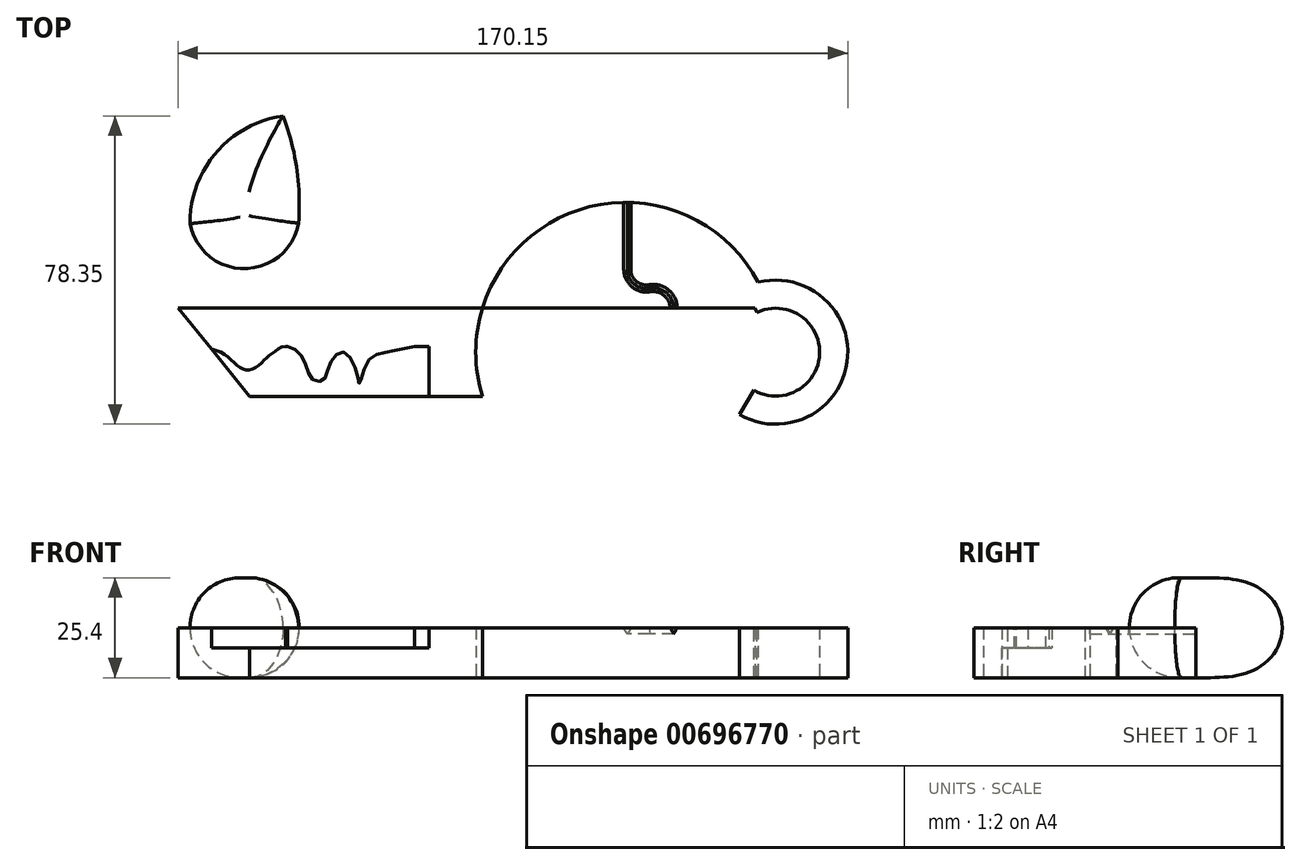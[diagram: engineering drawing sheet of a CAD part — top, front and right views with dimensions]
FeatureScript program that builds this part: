
annotation { "Feature Type Name" : "Feature", "Feature Type Description" : "" }
export const myFeature = defineFeature(function(context is Context, id is Id, definition is map)
    precondition{}
    {
        {
            var Q0;
            Q0=qCreatedBy(makeId("Top.planeOp"),FACE);
            var sketch = newSketch(context, id + "F0", { "sketchPlane" : qUnion([Q0])});
            skLineSegment(sketch, "E0", {"start": v(-76.55, 0) * mm, "end": v(76.12, 0) * mm});
            skLineSegment(sketch, "E1", {"start": v(0, 77.38) * mm, "end": v(0, -75.9) * mm});
            skLineSegment(sketch, "E2", {"start": v(0, 0) * mm, "end": v(76.12, 0) * mm});
            skLineSegment(sketch, "E3", {"start": v(38.06, 0) * mm, "end": v(38.06, 75.69) * mm});
            skCircle(sketch, "E4", {"center": v(38.06, 0) * mm, "radius": 38.06 * mm});
            skLineSegment(sketch, "E5.bottom", {"start": v(-75.64, 11.2) * mm, "end": v(74.43, 11.2) * mm});
            skLineSegment(sketch, "E5.top", {"start": v(-75.64, -11.2) * mm, "end": v(1.69, -11.2) * mm});
            skLineSegment(sketch, "E5.left", {"start": v(-75.64, 11.2) * mm, "end": v(-75.64, -11.2) * mm});
            skPoint(sketch, "E5.middle", {"position": v(0, 0) * mm});
            skCircle(sketch, "E6", {"center": v(48.41, -22.16) * mm, "radius": 17.71 * mm});
            skCircle(sketch, "E7.cCircle", {"center": v(15.13, -16.3) * mm, "radius": 9.61 * mm, "construction": true});
            skLineSegment(sketch, "E7.0", {"start": v(20.42, -7.35) * mm, "end": v(25.2, -13.71) * mm});
            skLineSegment(sketch, "E7.1", {"start": v(25.2, -13.71) * mm, "end": v(24.09, -21.6) * mm});
            skLineSegment(sketch, "E7.2", {"start": v(24.09, -21.6) * mm, "end": v(17.72, -26.38) * mm});
            skLineSegment(sketch, "E7.3", {"start": v(17.72, -26.38) * mm, "end": v(9.84, -25.26) * mm});
            skLineSegment(sketch, "E7.4", {"start": v(9.84, -25.26) * mm, "end": v(5.05, -18.9) * mm});
            skLineSegment(sketch, "E7.5", {"start": v(5.05, -18.9) * mm, "end": v(6.17, -11.01) * mm});
            skLineSegment(sketch, "E7.6", {"start": v(6.17, -11.01) * mm, "end": v(12.54, -6.23) * mm});
            skLineSegment(sketch, "E7.7", {"start": v(12.54, -6.23) * mm, "end": v(20.42, -7.35) * mm});
            skPoint(sketch, "E7.0.midPoint", {"position": v(22.81, -10.53) * mm});
            skArc(sketch, "E8", {"start": v(-48.97, 60.04) * mm, "mid": v(-65.9, 50.77) * mm, "end": v(-72.61, 32.66) * mm});
            skArc(sketch, "E9", {"start": v(-45.03, 32.74) * mm, "mid": v(-45.48, 46.61) * mm, "end": v(-48.97, 60.04) * mm});
            skArc(sketch, "E10", {"start": v(-72.61, 32.66) * mm, "mid": v(-58.79, 21.21) * mm, "end": v(-45.03, 32.74) * mm});
            skSolve(sketch);
        }
        {
            var Q0;
            {var subQ0=sQuery(id+"F0.wireOp",EDGE,"E4");var subQ1=sQuery(id+"F0.wireOp",EDGE,"E3");var subQ2=makeQuery(id+"F0.imprint","INTERSECT",VERTEX,{"derivedFrom":[subQ1,subQ0]});Q0=makeQuery(id+"F0.imprint","IMPRINT",FACE,{"disambiguationData":[TD([[makeQuery(id+"F0.imprint","IMPRINT",EDGE,{"disambiguationData":[TD([[subQ2,1.0]])],"derivedFrom":subQ1}),1.0]])]});}
            var Q1;
            {var subQ0=sQuery(id+"F0.wireOp",EDGE,"E4");var subQ1=sQuery(id+"F0.wireOp",EDGE,"E3");var subQ2=makeQuery(id+"F0.imprint","INTERSECT",VERTEX,{"derivedFrom":[subQ1,subQ0]});Q1=makeQuery(id+"F0.imprint","IMPRINT",FACE,{"disambiguationData":[TD([[makeQuery(id+"F0.imprint","IMPRINT",EDGE,{"disambiguationData":[TD([[subQ2,1.0]])],"derivedFrom":subQ1}),-1.0]])]});}
            var Q2;
            {var subQ0=sQuery(id+"F0.wireOp",EDGE,"E4");var subQ1=sQuery(id+"F0.wireOp",EDGE,"E2");var subQ2=makeQuery(id+"F0.imprint","INTERSECT",VERTEX,{"derivedFrom":[subQ1,subQ0]});Q2=makeQuery(id+"F0.imprint","IMPRINT",FACE,{"disambiguationData":[TD([[makeQuery(id+"F0.imprint","IMPRINT",EDGE,{"disambiguationData":[TD([[subQ2,1.0]])],"derivedFrom":subQ1}),1.0]])]});}
            var Q3;
            {var subQ1=sQuery(id+"F0.wireOp",EDGE,"E2");var subQ3=sQuery(id+"F0.wireOp",EDGE,"E3");var subQ4=makeQuery(id+"F0.imprint","INTERSECT",VERTEX,{"derivedFrom":[subQ1,subQ3]});Q3=makeQuery(id+"F0.imprint","IMPRINT",FACE,{"disambiguationData":[TD([[makeQuery(id+"F0.imprint","IMPRINT",EDGE,{"disambiguationData":[TD([[subQ4,-1.0]])],"derivedFrom":subQ3}),1.0]])]});}
            var Q4;
            {var subQ0=sQuery(id+"F0.wireOp",EDGE,"E4");var subQ1=sQuery(id+"F0.wireOp",EDGE,"E2");var subQ4=makeQuery(id+"F0.imprint","INTERSECT",VERTEX,{"derivedFrom":[subQ1,subQ0]});Q4=makeQuery(id+"F0.imprint","IMPRINT",FACE,{"disambiguationData":[TD([[makeQuery(id+"F0.imprint","IMPRINT",EDGE,{"disambiguationData":[TD([[subQ4,1.0]])],"derivedFrom":subQ1}),-1.0]])]});}
            var Q5;
            {var subQ3=sQuery(id+"F0.wireOp",EDGE,"E5.left");var subQ5=sQuery(id+"F0.wireOp",EDGE,"E5.top");var subQ6=makeQuery(id+"F0.imprint","INTERSECT",VERTEX,{"derivedFrom":[subQ5,subQ3]});Q5=makeQuery(id+"F0.imprint","IMPRINT",FACE,{"disambiguationData":[TD([[makeQuery(id+"F0.imprint","IMPRINT",EDGE,{"disambiguationData":[TD([[subQ6,-1.0]])],"derivedFrom":subQ5}),1.0]])]});}
            var Q6;
            {var subQ3=sQuery(id+"F0.wireOp",EDGE,"E5.left");var subQ5=sQuery(id+"F0.wireOp",EDGE,"E5.bottom");var subQ7=makeQuery(id+"F0.imprint","INTERSECT",VERTEX,{"derivedFrom":[subQ5,subQ3]});Q6=makeQuery(id+"F0.imprint","IMPRINT",FACE,{"disambiguationData":[TD([[makeQuery(id+"F0.imprint","IMPRINT",EDGE,{"disambiguationData":[TD([[subQ7,-1.0]])],"derivedFrom":subQ5}),-1.0]])]});}
            var Q7;
            {var subQ1=sQuery(id+"F0.wireOp",EDGE,"E1");var subQ3=sQuery(id+"F0.wireOp",EDGE,"E5.bottom");var subQ4=makeQuery(id+"F0.imprint","INTERSECT",VERTEX,{"derivedFrom":[subQ1,subQ3]});Q7=makeQuery(id+"F0.imprint","IMPRINT",FACE,{"disambiguationData":[TD([[makeQuery(id+"F0.imprint","IMPRINT",EDGE,{"disambiguationData":[TD([[subQ4,-1.0]])],"derivedFrom":subQ3}),-1.0]])]});}
            var Q8;
            {var subQ0=sQuery(id+"F0.wireOp",EDGE,"E4");var subQ3=sQuery(id+"F0.wireOp",EDGE,"E5.top");var subQ5=makeQuery(id+"F0.imprint","INTERSECT",VERTEX,{"derivedFrom":[subQ0,subQ3]});Q8=makeQuery(id+"F0.imprint","IMPRINT",FACE,{"disambiguationData":[TD([[makeQuery(id+"F0.imprint","IMPRINT",EDGE,{"disambiguationData":[TD([[subQ5,1.0]])],"derivedFrom":subQ3}),1.0]])]});}
            extrude(context, id + "F1", {"entities" : qUnion([Q0, Q1, Q2, Q3, Q4, Q5, Q6, Q7, Q8]), "depth" : 12.7 * mm, "offsetDistance" : 25.4 * mm});
        }
        {
            var Q0;
            Q0=makeQuery(id+"F1.opExtrude","SWEPT_FACE",FACE,{"disambiguationData":[OSD([sQuery(id+"F0.wireOp",EDGE,"E5.top")])]});
            var sketch = newSketch(context, id + "F2", { "sketchPlane" : qUnion([Q0])});
            skPoint(sketch, "E11.oppositeSnap0", {"position": v(1.69, 6.35) * mm});
            skLineSegment(sketch, "E12.bottom", {"start": v(-75.64, 12.7) * mm, "end": v(-11.84, 12.7) * mm});
            skLineSegment(sketch, "E12.top", {"start": v(-75.64, 7.53) * mm, "end": v(-11.84, 7.53) * mm});
            skLineSegment(sketch, "E12.left", {"start": v(-75.64, 12.7) * mm, "end": v(-75.64, 7.53) * mm});
            skLineSegment(sketch, "E12.right", {"start": v(-11.84, 12.7) * mm, "end": v(-11.84, 7.53) * mm});
            skSolve(sketch);
        }
        {
            var Q0;
            Q0=qSketchRegion(id+"F2",true);
            extrude(context, id + "F3", {"entities" : qUnion([Q0]), "operationType" : NewBodyOperationType.REMOVE, "oppositeDirection" : true, "depth" : 12.7 * mm, "offsetDistance" : 25.4 * mm});
        }
        {
            var Q0;
            Q0=makeQuery(id+"F3.boolean.opBoolean","COPY",FACE,{"derivedFrom":makeQuery(id+"F3.opExtrude","SWEPT_FACE",FACE,{"disambiguationData":[OSD([sQuery(id+"F2.wireOp",EDGE,"E12.top")])]})});
            var sketch = newSketch(context, id + "F4", { "sketchPlane" : qUnion([Q0])});
            skPoint(sketch, "E13.8.internal.snap0", {"position": v(-43.74, 1.5) * mm});
            skFitSpline(sketch, "E13", {"points": [v(-71.4, 1.5) * mm, v(-64.86, 0) * mm, v(-61.37, -2.73) * mm, v(-58.75, -4.47) * mm, v(-56.14, -4.03) * mm, v(-53.52, -1.85) * mm, v(-51.34, 0) * mm, v(-47.85, 1.5) * mm, v(-43.74, -1.85) * mm, v(-41.75, -6.65) * mm, v(-38.7, -7.09) * mm, v(-36.95, -2.73) * mm, v(-33.46, 0) * mm, v(-29.98, -6.21) * mm, v(-29.54, -7.96) * mm, v(-27.36, -2.29) * mm, v(-22.56, 0) * mm, v(-15.59, 1.5) * mm], "startDerivative": vector(98.42, -12.85) * mm, "endDerivative": vector(95.91, 21.9) * mm});
            skLineSegment(sketch, "E14", {"start": v(-71.4, 1.5) * mm, "end": v(-15.59, 1.5) * mm});
            skSolve(sketch);
        }
        {
            var Q0;
            {var subQ0=sQuery(id+"F4.wireOp",EDGE,"E14");var subQ1=sQuery(id+"F4.wireOp",EDGE,"E13");var subQ3=makeQuery(id+"F4.imprint","INTERSECT",VERTEX,{"disambiguationData":[OD(0.0)],"derivedFrom":[subQ1,subQ0]});Q0=makeQuery(id+"F4.imprint","IMPRINT",FACE,{"disambiguationData":[TD([[makeQuery(id+"F4.imprint","IMPRINT",EDGE,{"disambiguationData":[TD([[subQ3,1.0]])],"derivedFrom":subQ1}),1.0]])]});}
            var Q1;
            {var subQ0=sQuery(id+"F4.wireOp",EDGE,"E14");var subQ1=sQuery(id+"F4.wireOp",EDGE,"E13");var subQ3=makeQuery(id+"F4.imprint","INTERSECT",VERTEX,{"disambiguationData":[OD(1.0)],"derivedFrom":[subQ1,subQ0]});Q1=makeQuery(id+"F4.imprint","IMPRINT",FACE,{"disambiguationData":[TD([[makeQuery(id+"F4.imprint","IMPRINT",EDGE,{"disambiguationData":[TD([[subQ3,-1.0]])],"derivedFrom":subQ1}),1.0]])]});}
            var Q2;
            Q2=makeQuery(id+"F1.opExtrude","CAP_FACE",FACE,{"disambiguationData":[OSD([sQuery(id+"F0.wireOp",EDGE,"E4"),sQuery(id+"F0.wireOp",EDGE,"E5.bottom"),sQuery(id+"F0.wireOp",EDGE,"E5.top"),sQuery(id+"F0.wireOp",EDGE,"E5.left")])],"isStart":false});
            extrude(context, id + "F5", {"entities" : qUnion([Q0, Q1]), "operationType" : NewBodyOperationType.ADD, "endBound" : BoundingType.UP_TO_SURFACE, "depth" : 25.4 * mm, "endBoundEntityFace" : qUnion([Q2]), "offsetDistance" : 25.4 * mm});
        }
        {
            var Q0;
            {var subQ0=sQuery(id+"F0.wireOp",EDGE,"E5.left");var subQ1=sQuery(id+"F0.wireOp",EDGE,"E5.top");var subQ2=sQuery(id+"F0.wireOp",EDGE,"E5.bottom");var subQ3=sQuery(id+"F0.wireOp",EDGE,"E4");Q0=makeQuery(id+"F5.boolean.opBoolean","MERGE",FACE,{"derivedFrom":[makeQuery(id+"F1.opExtrude","CAP_FACE",FACE,{"disambiguationData":[OSD([subQ3,subQ2,subQ1,subQ0])],"isStart":false}),makeQuery(id+"F5.opExtrude","CAP_FACE",FACE,{"disambiguationData":[OSD([subQ3,subQ2,subQ1,subQ0]),OD(0.0)],"isStart":false}),makeQuery(id+"F5.opExtrude","CAP_FACE",FACE,{"disambiguationData":[OSD([subQ3,subQ2,subQ1,subQ0]),OD(1.0)],"isStart":false})]});}
            var sketch = newSketch(context, id + "F6", { "sketchPlane" : qUnion([Q0])});
            skLineSegment(sketch, "E15", {"start": v(-54.4, -14.93) * mm, "end": v(-80.56, -12.75) * mm});
            skLineSegment(sketch, "E16", {"start": v(-80.56, -12.75) * mm, "end": v(-75.64, 11.2) * mm});
            skLineSegment(sketch, "E17", {"start": v(-75.64, 11.2) * mm, "end": v(-54.4, -14.93) * mm});
            skSolve(sketch);
        }
        {
            var Q0;
            Q0=qSketchRegion(id+"F6",true);
            extrude(context, id + "F7", {"entities" : qUnion([Q0]), "operationType" : NewBodyOperationType.REMOVE, "endBound" : BoundingType.THROUGH_ALL, "oppositeDirection" : true, "depth" : 25.4 * mm, "offsetDistance" : 25.4 * mm});
        }
        {
            var Q0;
            Q0=qCreatedBy(makeId("Right.planeOp"),FACE);
            cPlane(context, id + "F8", {"entities" : qUnion([Q0]), "cplaneType" : CPlaneType.OFFSET, "offset" : 76.2 * mm, "width" : 152.4 * mm, "height" : 152.4 * mm});
        }
        {
            var Q0;
            Q0=qCreatedBy(id+"F8.planeOp",FACE);
            var sketch = newSketch(context, id + "F9", { "sketchPlane" : qUnion([Q0])});
            skLineSegment(sketch, "E18", {"start": v(0, -5.67) * mm, "end": v(0, 19.48) * mm});
            skLineSegment(sketch, "E19.top", {"start": v(11.16, 0) * mm, "end": v(18.3, 0) * mm});
            skLineSegment(sketch, "E20", {"start": v(11.16, 0) * mm, "end": v(11.16, 12.7) * mm});
            skLineSegment(sketch, "E21", {"start": v(11.16, 12.7) * mm, "end": v(18.3, 12.7) * mm});
            skLineSegment(sketch, "E22", {"start": v(18.3, 12.7) * mm, "end": v(18.3, 0) * mm});
            skSolve(sketch);
        }
        {
            var Q0;
            Q0=makeQuery(id+"F9.imprint","IMPRINT",FACE,{"disambiguationData":[TD([[makeQuery(id+"F9.imprint","IMPRINT",EDGE,{"derivedFrom":sQuery(id+"F9.wireOp",EDGE,"E19.top")}),1.0]])]});
            var Q1;
            Q1=sQuery(id+"F9.wireOp",EDGE,"E18");
            revolve(context, id + "F10", {"operationType" : NewBodyOperationType.ADD, "entities" : qUnion([Q0]), "axis" : qUnion([Q1]), "revolveType" : RevolveType.TWO_DIRECTIONS, "angle" : 25 * degree, "angleBack" : 150 * degree});
        }
        {
            var Q0;
            Q0=qCreatedBy(makeId("Front.planeOp"),FACE);
            cPlane(context, id + "F11", {"entities" : qUnion([Q0]), "cplaneType" : CPlaneType.OFFSET, "offset" : 38.1 * mm, "width" : 152.4 * mm, "height" : 152.4 * mm});
        }
        {
            var Q0;
            {var subQ0=sQuery(id+"F0.wireOp",EDGE,"E5.left");var subQ1=sQuery(id+"F0.wireOp",EDGE,"E5.top");var subQ2=sQuery(id+"F0.wireOp",EDGE,"E5.bottom");var subQ3=sQuery(id+"F0.wireOp",EDGE,"E4");Q0=makeQuery(id+"F5.boolean.opBoolean","MERGE",FACE,{"derivedFrom":[makeQuery(id+"F1.opExtrude","CAP_FACE",FACE,{"disambiguationData":[OSD([subQ3,subQ2,subQ1,subQ0])],"isStart":false}),makeQuery(id+"F5.opExtrude","CAP_FACE",FACE,{"disambiguationData":[OSD([subQ3,subQ2,subQ1,subQ0]),OD(0.0)],"isStart":false}),makeQuery(id+"F5.opExtrude","CAP_FACE",FACE,{"disambiguationData":[OSD([subQ3,subQ2,subQ1,subQ0]),OD(1.0)],"isStart":false})]});}
            var sketch = newSketch(context, id + "F12", { "sketchPlane" : qUnion([Q0])});
            skLineSegment(sketch, "E23", {"start": v(38.5, -38.06) * mm, "end": v(38.5, -21.04) * mm});
            skArc(sketch, "E24", {"start": v(38.5, -21.04) * mm, "mid": v(40.22, -17.32) * mm, "end": v(44.17, -16.24) * mm});
            skArc(sketch, "E25", {"start": v(44.17, -16.24) * mm, "mid": v(48.62, -14.91) * mm, "end": v(50.28, -10.57) * mm});
            skLineSegment(sketch, "E26", {"start": v(50.28, -10.57) * mm, "end": v(50.28, 0) * mm});
            skLineSegment(sketch, "E27", {"start": v(0, 0) * mm, "end": v(43.3, 0) * mm});
            skLineSegment(sketch, "E28.MirrorCS", {"start": v(50.28, 10.57) * mm, "end": v(50.28, 0) * mm});
            skArc(sketch, "E29.MirrorCS", {"start": v(44.17, 16.24) * mm, "mid": v(48.62, 14.91) * mm, "end": v(50.28, 10.57) * mm});
            skArc(sketch, "E30.MirrorCS", {"start": v(38.5, 21.04) * mm, "mid": v(40.22, 17.32) * mm, "end": v(44.17, 16.24) * mm});
            skLineSegment(sketch, "E31.MirrorCS", {"start": v(38.5, 38.06) * mm, "end": v(38.5, 21.04) * mm});
            skSolve(sketch);
        }
        {
            var Q0;
            Q0=qCreatedBy(id+"F11.planeOp",FACE);
            var sketch = newSketch(context, id + "F13", { "sketchPlane" : qUnion([Q0])});
            skCircle(sketch, "E32.cCircle", {"center": v(38.5, 12.73) * mm, "radius": 1.6 * mm, "construction": true});
            skLineSegment(sketch, "E32.0", {"start": v(38.5, 11.14) * mm, "end": v(37.1, 13.53) * mm});
            skLineSegment(sketch, "E32.1", {"start": v(37.1, 13.53) * mm, "end": v(39.87, 13.53) * mm});
            skLineSegment(sketch, "E32.2", {"start": v(39.87, 13.53) * mm, "end": v(38.5, 11.14) * mm});
            skSolve(sketch);
        }
        {
            var Q0;
            Q0=makeQuery(id+"F13.imprint","IMPRINT",FACE,{"disambiguationData":[TD([[makeQuery(id+"F13.imprint","IMPRINT",EDGE,{"derivedFrom":sQuery(id+"F13.wireOp",EDGE,"E32.0")}),-1.0]])]});
            var Q1;
            Q1=sQuery(id+"F12.wireOp",EDGE,"E23");
            var Q2;
            Q2=sQuery(id+"F12.wireOp",EDGE,"E24");
            var Q3;
            Q3=sQuery(id+"F12.wireOp",EDGE,"E25");
            var Q4;
            Q4=sQuery(id+"F12.wireOp",EDGE,"E26");
            var Q5;
            Q5=sQuery(id+"F12.wireOp",EDGE,"E28.MirrorCS");
            var Q6;
            Q6=sQuery(id+"F12.wireOp",EDGE,"E29.MirrorCS");
            var Q7;
            Q7=sQuery(id+"F12.wireOp",EDGE,"E30.MirrorCS");
            var Q8;
            Q8=sQuery(id+"F12.wireOp",EDGE,"E31.MirrorCS");
            sweep(context, id + "F14", {"operationType" : NewBodyOperationType.REMOVE, "profiles" : qUnion([Q0]), "path" : qUnion([Q1, Q2, Q3, Q4, Q5, Q6, Q7, Q8])});
        }
        {
            var Q0;
            Q0=makeQuery(id+"F0.imprint","IMPRINT",FACE,{"disambiguationData":[TD([[makeQuery(id+"F0.imprint","IMPRINT",EDGE,{"derivedFrom":sQuery(id+"F0.wireOp",EDGE,"E8")}),1.0]])]});
            extrude(context, id + "F15", {"entities" : qUnion([Q0]), "depth" : 25.4 * mm, "offsetDistance" : 25.4 * mm});
        }
        {
            var Q0;
            Q0=makeQuery(id+"F15.opExtrude","CAP_FACE",FACE,{"disambiguationData":[OSD([sQuery(id+"F0.wireOp",EDGE,"E8"),sQuery(id+"F0.wireOp",EDGE,"E9"),sQuery(id+"F0.wireOp",EDGE,"E10")])],"isStart":false});
            var Q1;
            Q1=makeQuery(id+"F15.opExtrude","CAP_FACE",FACE,{"disambiguationData":[OSD([sQuery(id+"F0.wireOp",EDGE,"E8"),sQuery(id+"F0.wireOp",EDGE,"E9"),sQuery(id+"F0.wireOp",EDGE,"E10")])],"isStart":true});
            fillet(context, id + "F16", {"entities" : qUnion([Q0, Q1]), "radius" : 12.7 * mm, "tangentPropagation" : true, "allowEdgeOverflow" : false});
        }
    });
